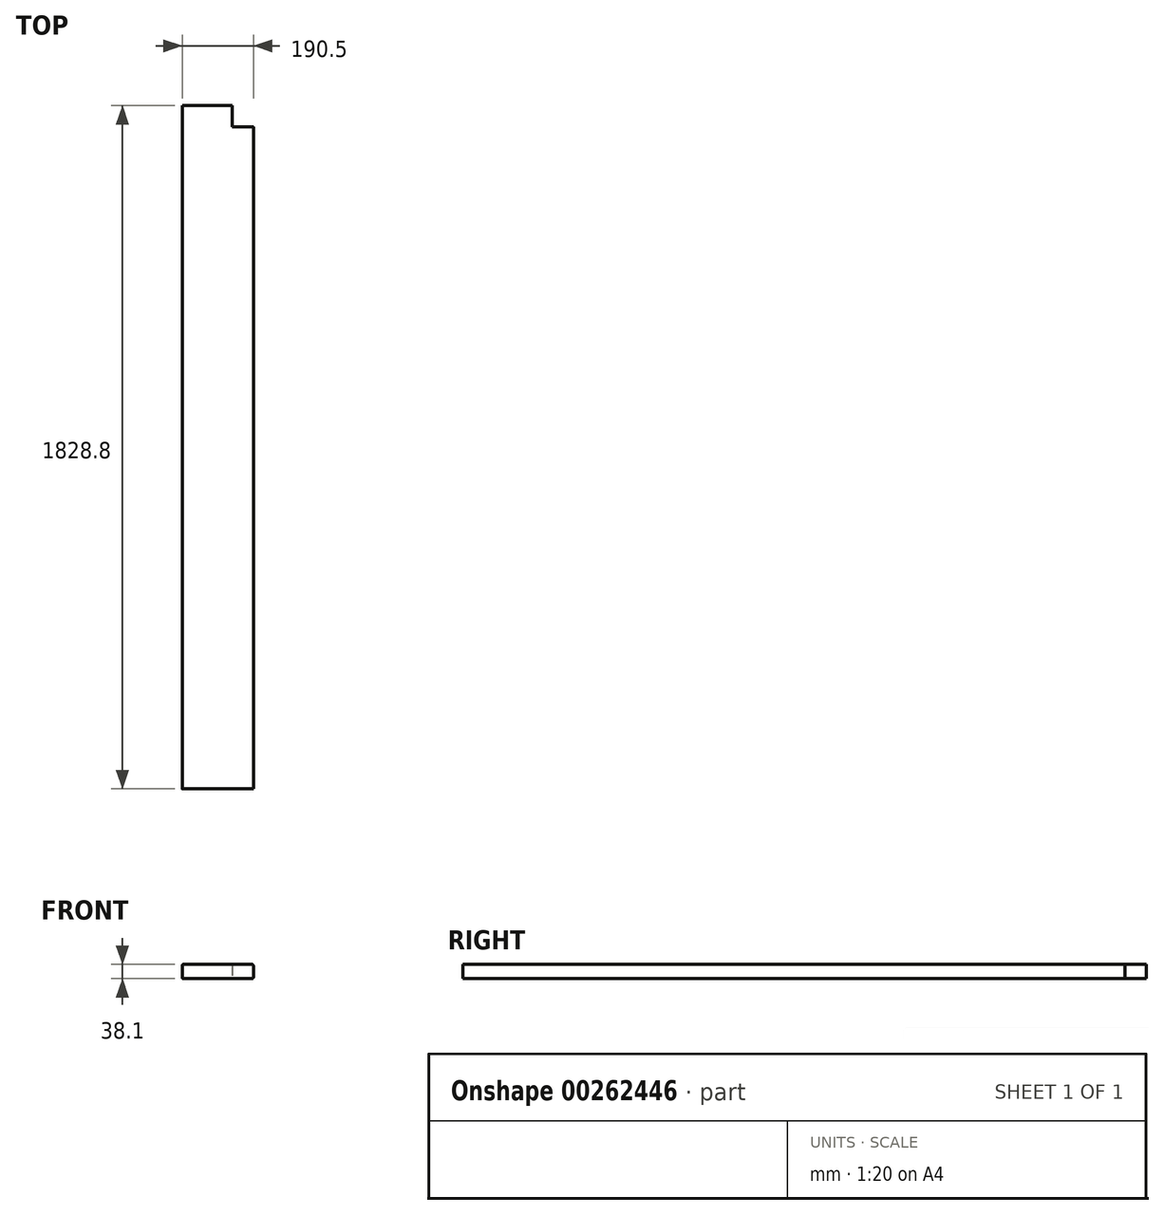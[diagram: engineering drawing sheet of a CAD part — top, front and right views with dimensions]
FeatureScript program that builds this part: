
annotation { "Feature Type Name" : "Feature", "Feature Type Description" : "" }
export const myFeature = defineFeature(function(context is Context, id is Id, definition is map)
    precondition{}
    {
        {
            var Q0;
            Q0=qCreatedBy(makeId("Front.planeOp"),FACE);
            var sketch = newSketch(context, id + "F0", { "sketchPlane" : qUnion([Q0])});
            skLineSegment(sketch, "E0.bottom", {"start": v(92.07, 19.05) * mm, "end": v(-92.08, 19.05) * mm});
            skLineSegment(sketch, "E0.top", {"start": v(92.08, -19.05) * mm, "end": v(-92.08, -19.05) * mm});
            skLineSegment(sketch, "E0.left", {"start": v(95.25, 15.87) * mm, "end": v(95.25, -15.88) * mm});
            skLineSegment(sketch, "E0.right", {"start": v(-95.25, 15.87) * mm, "end": v(-95.25, -15.88) * mm});
            skPoint(sketch, "E0.middle", {"position": v(0, 0) * mm});
            skPoint(sketch, "E1.visualSharp", {"position": v(-95.25, 19.05) * mm});
            skArc(sketch, "E1.filletArc", {"start": v(-92.08, 19.05) * mm, "mid": v(-94.32, 18.12) * mm, "end": v(-95.25, 15.87) * mm});
            skPoint(sketch, "E2.visualSharp", {"position": v(-95.25, -19.05) * mm});
            skArc(sketch, "E2.filletArc", {"start": v(-95.25, -15.88) * mm, "mid": v(-94.32, -18.12) * mm, "end": v(-92.08, -19.05) * mm});
            skPoint(sketch, "E3.visualSharp", {"position": v(95.25, 19.05) * mm});
            skArc(sketch, "E3.filletArc", {"start": v(95.25, 15.87) * mm, "mid": v(94.32, 18.12) * mm, "end": v(92.07, 19.05) * mm});
            skPoint(sketch, "E4.visualSharp", {"position": v(95.25, -19.05) * mm});
            skArc(sketch, "E4.filletArc", {"start": v(92.08, -19.05) * mm, "mid": v(94.32, -18.12) * mm, "end": v(95.25, -15.88) * mm});
            skSolve(sketch);
        }
        {
            var Q0;
            Q0=makeQuery(id+"F0.imprint","IMPRINT",FACE,{"disambiguationData":[TD([[makeQuery(id+"F0.imprint","IMPRINT",EDGE,{"derivedFrom":sQuery(id+"F0.wireOp",EDGE,"E0.bottom")}),1.0]])]});
            extrude(context, id + "F1", {"entities" : qUnion([Q0]), "depth" : 1828.8 * mm});
        }
        {
            var Q0;
            Q0=qCreatedBy(makeId("Top.planeOp"),FACE);
            var sketch = newSketch(context, id + "F2", { "sketchPlane" : qUnion([Q0])});
            skLineSegment(sketch, "E5.bottom", {"start": v(95.25, 0) * mm, "end": v(38.1, 0) * mm});
            skLineSegment(sketch, "E5.top", {"start": v(95.25, -57.15) * mm, "end": v(38.1, -57.15) * mm});
            skLineSegment(sketch, "E5.left", {"start": v(95.25, 0) * mm, "end": v(95.25, -57.15) * mm});
            skLineSegment(sketch, "E5.right", {"start": v(38.1, 0) * mm, "end": v(38.1, -57.15) * mm});
            skPoint(sketch, "E5.middle", {"position": v(66.67, -28.58) * mm});
            skSolve(sketch);
        }
        {
            var Q0;
            Q0 = qSketchRegion(id + "F2", true);
            extrude(context, id + "F3", {"entities" : qUnion([Q0]), "operationType" : NewBodyOperationType.REMOVE, "endBound" : BoundingType.THROUGH_ALL, "depth" : 25.4 * mm, "hasSecondDirection" : true, "secondDirectionBound" : SecondDirectionBoundingType.THROUGH_ALL, "secondDirectionOppositeDirection" : true, "secondDirectionDepth" : 25.4 * mm});
        }
    });
